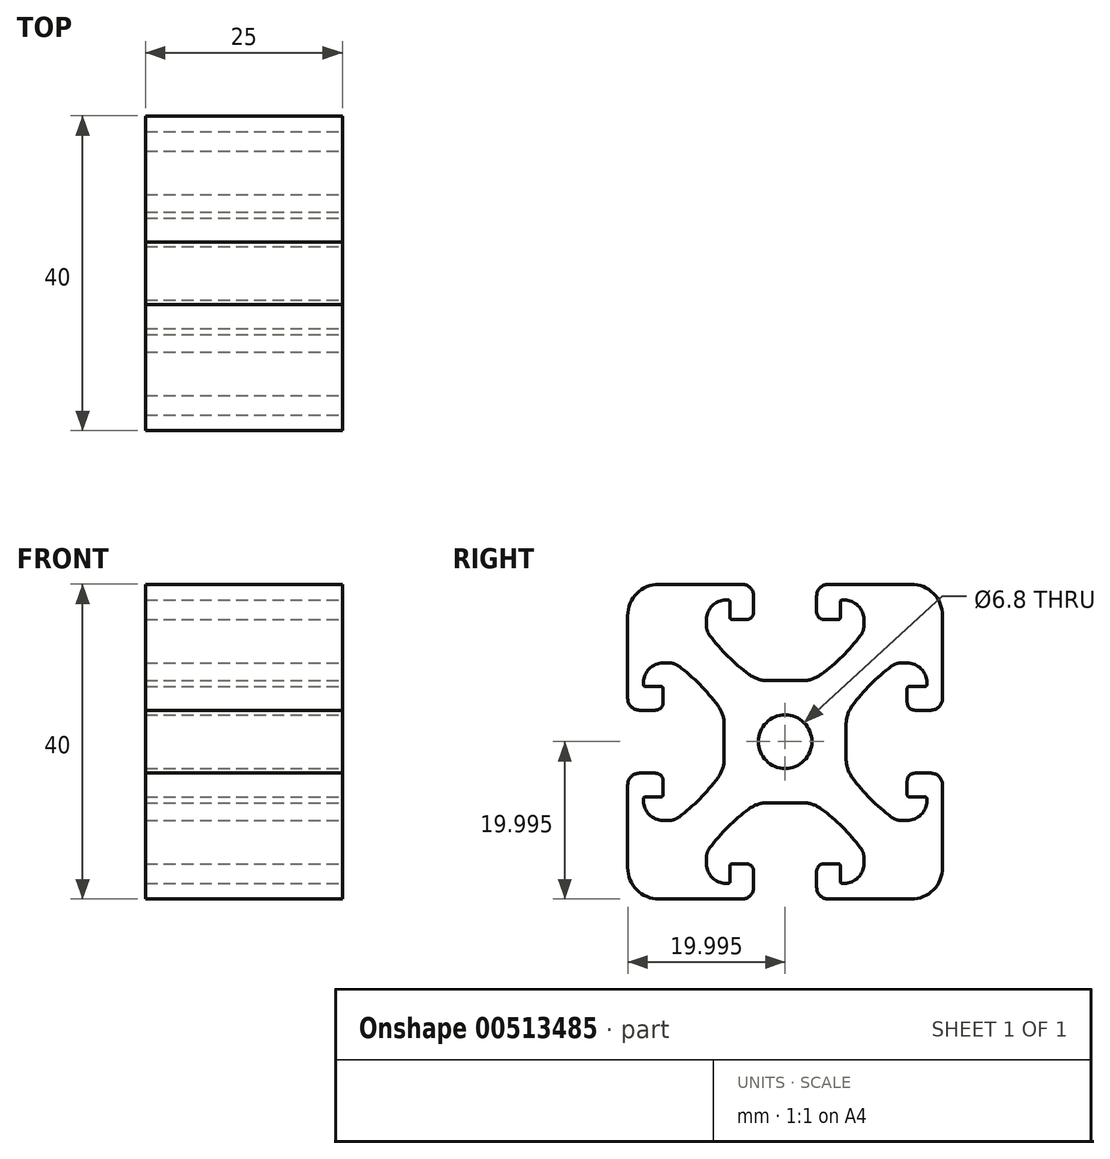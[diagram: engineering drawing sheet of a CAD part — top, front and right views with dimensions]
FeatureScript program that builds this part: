
annotation { "Feature Type Name" : "Feature", "Feature Type Description" : "" }
export const myFeature = defineFeature(function(context is Context, id is Id, definition is map)
    precondition{}
    {
        {
            var Q0;
            Q0=qCreatedBy(makeId("Right.planeOp"),FACE);
            var sketch = newSketch(context, id + "F0", { "sketchPlane" : qUnion([Q0])});
            skArc(sketch, "E0.0.0", {"start": v(4.09, -18.51) * mm, "mid": v(4.52, -19.58) * mm, "end": v(5.59, -20.01) * mm});
            skLineSegment(sketch, "E0.0.1", {"start": v(5.59, -20.01) * mm, "end": v(16.09, -20.01) * mm});
            skArc(sketch, "E0.0.2", {"start": v(16.09, -20.01) * mm, "mid": v(18.91, -18.84) * mm, "end": v(20.09, -16.01) * mm});
            skLineSegment(sketch, "E0.0.3", {"start": v(20.09, -16.01) * mm, "end": v(20.09, -5.51) * mm});
            skArc(sketch, "E0.0.4", {"start": v(20.09, -5.51) * mm, "mid": v(19.65, -4.45) * mm, "end": v(18.59, -4.01) * mm});
            skLineSegment(sketch, "E0.0.5", {"start": v(18.59, -4.01) * mm, "end": v(16.59, -4.01) * mm});
            skArc(sketch, "E0.0.6", {"start": v(16.59, -4.01) * mm, "mid": v(15.88, -4.3) * mm, "end": v(15.59, -5.01) * mm});
            skLineSegment(sketch, "E0.0.7", {"start": v(15.59, -5.01) * mm, "end": v(15.59, -6.76) * mm});
            skArc(sketch, "E0.0.8", {"start": v(15.59, -6.76) * mm, "mid": v(15.66, -6.94) * mm, "end": v(15.84, -7.01) * mm});
            skLineSegment(sketch, "E0.0.9", {"start": v(15.84, -7.01) * mm, "end": v(17.84, -7.01) * mm});
            skArc(sketch, "E0.0.10", {"start": v(17.84, -7.01) * mm, "mid": v(18.01, -7.09) * mm, "end": v(18.09, -7.26) * mm});
            skLineSegment(sketch, "E0.0.11", {"start": v(18.09, -7.26) * mm, "end": v(18.09, -7.51) * mm});
            skArc(sketch, "E0.0.12", {"start": v(18.09, -7.51) * mm, "mid": v(17.35, -9.28) * mm, "end": v(15.59, -10.01) * mm});
            skLineSegment(sketch, "E0.0.13", {"start": v(15.59, -10.01) * mm, "end": v(14.8, -10.01) * mm});
            skArc(sketch, "E0.0.14", {"start": v(14.8, -10.01) * mm, "mid": v(14.17, -9.91) * mm, "end": v(13.6, -9.6) * mm});
            skArc(sketch, "E0.0.15", {"start": v(13.6, -9.6) * mm, "mid": v(10.93, -7.28) * mm, "end": v(8.63, -4.6) * mm});
            skArc(sketch, "E0.0.16", {"start": v(8.63, -4.6) * mm, "mid": v(8.04, -3.47) * mm, "end": v(7.84, -2.2) * mm});
            skLineSegment(sketch, "E0.0.17", {"start": v(7.84, -2.2) * mm, "end": v(7.84, 2.18) * mm});
            skArc(sketch, "E0.0.18", {"start": v(7.84, 2.18) * mm, "mid": v(8.04, 3.44) * mm, "end": v(8.63, 4.57) * mm});
            skArc(sketch, "E0.0.19", {"start": v(8.63, 4.57) * mm, "mid": v(10.93, 7.25) * mm, "end": v(13.6, 9.58) * mm});
            skArc(sketch, "E0.0.20", {"start": v(13.6, 9.58) * mm, "mid": v(14.17, 9.88) * mm, "end": v(14.8, 9.99) * mm});
            skLineSegment(sketch, "E0.0.21", {"start": v(14.8, 9.99) * mm, "end": v(15.59, 9.99) * mm});
            skArc(sketch, "E0.0.22", {"start": v(15.59, 9.99) * mm, "mid": v(17.35, 9.25) * mm, "end": v(18.09, 7.49) * mm});
            skLineSegment(sketch, "E0.0.23", {"start": v(18.09, 7.49) * mm, "end": v(18.09, 7.24) * mm});
            skArc(sketch, "E0.0.24", {"start": v(18.09, 7.24) * mm, "mid": v(18.01, 7.06) * mm, "end": v(17.84, 6.99) * mm});
            skLineSegment(sketch, "E0.0.25", {"start": v(17.84, 6.99) * mm, "end": v(15.84, 6.99) * mm});
            skArc(sketch, "E0.0.26", {"start": v(15.84, 6.99) * mm, "mid": v(15.66, 6.91) * mm, "end": v(15.59, 6.74) * mm});
            skLineSegment(sketch, "E0.0.27", {"start": v(15.59, 6.74) * mm, "end": v(15.59, 4.99) * mm});
            skArc(sketch, "E0.0.28", {"start": v(15.59, 4.99) * mm, "mid": v(15.88, 4.28) * mm, "end": v(16.59, 3.99) * mm});
            skLineSegment(sketch, "E0.0.29", {"start": v(16.59, 3.99) * mm, "end": v(18.59, 3.99) * mm});
            skArc(sketch, "E0.0.30", {"start": v(18.59, 3.99) * mm, "mid": v(19.65, 4.42) * mm, "end": v(20.09, 5.49) * mm});
            skLineSegment(sketch, "E0.0.31", {"start": v(20.09, 5.49) * mm, "end": v(20.09, 15.99) * mm});
            skArc(sketch, "E0.0.32", {"start": v(20.09, 15.99) * mm, "mid": v(18.91, 18.81) * mm, "end": v(16.09, 19.99) * mm});
            skLineSegment(sketch, "E0.0.33", {"start": v(16.09, 19.99) * mm, "end": v(5.59, 19.99) * mm});
            skArc(sketch, "E0.0.34", {"start": v(5.59, 19.99) * mm, "mid": v(4.52, 19.55) * mm, "end": v(4.09, 18.49) * mm});
            skLineSegment(sketch, "E0.0.35", {"start": v(4.09, 18.49) * mm, "end": v(4.09, 16.49) * mm});
            skArc(sketch, "E0.0.36", {"start": v(4.09, 16.49) * mm, "mid": v(4.38, 15.78) * mm, "end": v(5.09, 15.49) * mm});
            skLineSegment(sketch, "E0.0.37", {"start": v(5.09, 15.49) * mm, "end": v(6.84, 15.49) * mm});
            skArc(sketch, "E0.0.38", {"start": v(6.84, 15.49) * mm, "mid": v(7.01, 15.56) * mm, "end": v(7.09, 15.74) * mm});
            skLineSegment(sketch, "E0.0.39", {"start": v(7.09, 15.74) * mm, "end": v(7.09, 17.74) * mm});
            skArc(sketch, "E0.0.40", {"start": v(7.09, 17.74) * mm, "mid": v(7.16, 17.91) * mm, "end": v(7.34, 17.99) * mm});
            skLineSegment(sketch, "E0.0.41", {"start": v(7.34, 17.99) * mm, "end": v(7.59, 17.99) * mm});
            skArc(sketch, "E0.0.42", {"start": v(7.59, 17.99) * mm, "mid": v(9.35, 17.25) * mm, "end": v(10.09, 15.49) * mm});
            skLineSegment(sketch, "E0.0.43", {"start": v(10.09, 15.49) * mm, "end": v(10.09, 14.7) * mm});
            skArc(sketch, "E0.0.44", {"start": v(10.09, 14.7) * mm, "mid": v(9.98, 14.07) * mm, "end": v(9.68, 13.5) * mm});
            skArc(sketch, "E0.0.45", {"start": v(9.68, 13.5) * mm, "mid": v(7.35, 10.83) * mm, "end": v(4.67, 8.53) * mm});
            skArc(sketch, "E0.0.46", {"start": v(4.67, 8.53) * mm, "mid": v(3.54, 7.94) * mm, "end": v(2.28, 7.74) * mm});
            skLineSegment(sketch, "E0.0.47", {"start": v(2.28, 7.74) * mm, "end": v(-2.1, 7.74) * mm});
            skArc(sketch, "E0.0.48", {"start": v(-2.1, 7.74) * mm, "mid": v(-3.37, 7.94) * mm, "end": v(-4.5, 8.53) * mm});
            skArc(sketch, "E0.0.49", {"start": v(-4.5, 8.53) * mm, "mid": v(-7.18, 10.83) * mm, "end": v(-9.5, 13.5) * mm});
            skArc(sketch, "E0.0.50", {"start": v(-9.5, 13.5) * mm, "mid": v(-9.81, 14.07) * mm, "end": v(-9.91, 14.7) * mm});
            skLineSegment(sketch, "E0.0.51", {"start": v(-9.91, 14.7) * mm, "end": v(-9.91, 15.49) * mm});
            skArc(sketch, "E0.0.52", {"start": v(-9.91, 15.49) * mm, "mid": v(-9.18, 17.25) * mm, "end": v(-7.41, 17.99) * mm});
            skLineSegment(sketch, "E0.0.53", {"start": v(-7.41, 17.99) * mm, "end": v(-7.16, 17.99) * mm});
            skArc(sketch, "E0.0.54", {"start": v(-7.16, 17.99) * mm, "mid": v(-6.99, 17.91) * mm, "end": v(-6.91, 17.74) * mm});
            skLineSegment(sketch, "E0.0.55", {"start": v(-6.91, 17.74) * mm, "end": v(-6.91, 15.74) * mm});
            skArc(sketch, "E0.0.56", {"start": v(-6.91, 15.74) * mm, "mid": v(-6.84, 15.56) * mm, "end": v(-6.66, 15.49) * mm});
            skLineSegment(sketch, "E0.0.57", {"start": v(-6.66, 15.49) * mm, "end": v(-4.91, 15.49) * mm});
            skArc(sketch, "E0.0.58", {"start": v(-4.91, 15.49) * mm, "mid": v(-4.2, 15.78) * mm, "end": v(-3.91, 16.49) * mm});
            skLineSegment(sketch, "E0.0.59", {"start": v(-3.91, 16.49) * mm, "end": v(-3.91, 18.49) * mm});
            skArc(sketch, "E0.0.60", {"start": v(-3.91, 18.49) * mm, "mid": v(-4.35, 19.55) * mm, "end": v(-5.41, 19.99) * mm});
            skLineSegment(sketch, "E0.0.61", {"start": v(-5.41, 19.99) * mm, "end": v(-15.91, 19.99) * mm});
            skArc(sketch, "E0.0.62", {"start": v(-15.91, 19.99) * mm, "mid": v(-18.74, 18.81) * mm, "end": v(-19.91, 15.99) * mm});
            skLineSegment(sketch, "E0.0.63", {"start": v(-19.91, 15.99) * mm, "end": v(-19.91, 5.49) * mm});
            skArc(sketch, "E0.0.64", {"start": v(-19.91, 5.49) * mm, "mid": v(-19.48, 4.42) * mm, "end": v(-18.41, 3.99) * mm});
            skLineSegment(sketch, "E0.0.65", {"start": v(-18.41, 3.99) * mm, "end": v(-16.41, 3.99) * mm});
            skArc(sketch, "E0.0.66", {"start": v(-16.41, 3.99) * mm, "mid": v(-15.7, 4.28) * mm, "end": v(-15.41, 4.99) * mm});
            skLineSegment(sketch, "E0.0.67", {"start": v(-15.41, 4.99) * mm, "end": v(-15.41, 6.74) * mm});
            skArc(sketch, "E0.0.68", {"start": v(-15.41, 6.74) * mm, "mid": v(-15.49, 6.91) * mm, "end": v(-15.66, 6.99) * mm});
            skLineSegment(sketch, "E0.0.69", {"start": v(-15.66, 6.99) * mm, "end": v(-17.66, 6.99) * mm});
            skArc(sketch, "E0.0.70", {"start": v(-17.66, 6.99) * mm, "mid": v(-17.84, 7.06) * mm, "end": v(-17.91, 7.24) * mm});
            skLineSegment(sketch, "E0.0.71", {"start": v(-17.91, 7.24) * mm, "end": v(-17.91, 7.49) * mm});
            skArc(sketch, "E0.0.72", {"start": v(-17.91, 7.49) * mm, "mid": v(-17.18, 9.25) * mm, "end": v(-15.41, 9.99) * mm});
            skLineSegment(sketch, "E0.0.73", {"start": v(-15.41, 9.99) * mm, "end": v(-14.64, 9.99) * mm});
            skArc(sketch, "E0.0.74", {"start": v(-14.64, 9.99) * mm, "mid": v(-14, 9.88) * mm, "end": v(-13.43, 9.58) * mm});
            skArc(sketch, "E0.0.75", {"start": v(-13.43, 9.58) * mm, "mid": v(-10.76, 7.25) * mm, "end": v(-8.46, 4.57) * mm});
            skArc(sketch, "E0.0.76", {"start": v(-8.46, 4.57) * mm, "mid": v(-7.87, 3.44) * mm, "end": v(-7.66, 2.18) * mm});
            skLineSegment(sketch, "E0.0.77", {"start": v(-7.66, 2.18) * mm, "end": v(-7.66, -2.2) * mm});
            skArc(sketch, "E0.0.78", {"start": v(-7.66, -2.2) * mm, "mid": v(-7.87, -3.47) * mm, "end": v(-8.46, -4.6) * mm});
            skArc(sketch, "E0.0.79", {"start": v(-8.46, -4.6) * mm, "mid": v(-10.76, -7.28) * mm, "end": v(-13.43, -9.6) * mm});
            skArc(sketch, "E0.0.80", {"start": v(-13.43, -9.6) * mm, "mid": v(-14, -9.91) * mm, "end": v(-14.64, -10.01) * mm});
            skLineSegment(sketch, "E0.0.81", {"start": v(-14.64, -10.01) * mm, "end": v(-15.41, -10.01) * mm});
            skArc(sketch, "E0.0.82", {"start": v(-15.41, -10.01) * mm, "mid": v(-17.18, -9.28) * mm, "end": v(-17.91, -7.51) * mm});
            skLineSegment(sketch, "E0.0.83", {"start": v(-17.91, -7.51) * mm, "end": v(-17.91, -7.26) * mm});
            skArc(sketch, "E0.0.84", {"start": v(-17.91, -7.26) * mm, "mid": v(-17.84, -7.09) * mm, "end": v(-17.66, -7.01) * mm});
            skLineSegment(sketch, "E0.0.85", {"start": v(-17.66, -7.01) * mm, "end": v(-15.66, -7.01) * mm});
            skArc(sketch, "E0.0.86", {"start": v(-15.66, -7.01) * mm, "mid": v(-15.49, -6.94) * mm, "end": v(-15.41, -6.76) * mm});
            skLineSegment(sketch, "E0.0.87", {"start": v(-15.41, -6.76) * mm, "end": v(-15.41, -5.01) * mm});
            skArc(sketch, "E0.0.88", {"start": v(-15.41, -5.01) * mm, "mid": v(-15.7, -4.3) * mm, "end": v(-16.41, -4.01) * mm});
            skLineSegment(sketch, "E0.0.89", {"start": v(-16.41, -4.01) * mm, "end": v(-18.41, -4.01) * mm});
            skArc(sketch, "E0.0.90", {"start": v(-18.41, -4.01) * mm, "mid": v(-19.48, -4.45) * mm, "end": v(-19.91, -5.51) * mm});
            skLineSegment(sketch, "E0.0.91", {"start": v(-19.91, -5.51) * mm, "end": v(-19.91, -16.01) * mm});
            skArc(sketch, "E0.0.92", {"start": v(-19.91, -16.01) * mm, "mid": v(-18.74, -18.84) * mm, "end": v(-15.91, -20.01) * mm});
            skLineSegment(sketch, "E0.0.93", {"start": v(-15.91, -20.01) * mm, "end": v(-5.41, -20.01) * mm});
            skArc(sketch, "E0.0.94", {"start": v(-5.41, -20.01) * mm, "mid": v(-4.35, -19.58) * mm, "end": v(-3.91, -18.51) * mm});
            skLineSegment(sketch, "E0.0.95", {"start": v(-3.91, -18.51) * mm, "end": v(-3.91, -16.51) * mm});
            skArc(sketch, "E0.0.96", {"start": v(-3.91, -16.51) * mm, "mid": v(-4.2, -15.8) * mm, "end": v(-4.91, -15.51) * mm});
            skLineSegment(sketch, "E0.0.97", {"start": v(-4.91, -15.51) * mm, "end": v(-6.66, -15.51) * mm});
            skArc(sketch, "E0.0.98", {"start": v(-6.66, -15.51) * mm, "mid": v(-6.84, -15.59) * mm, "end": v(-6.91, -15.76) * mm});
            skLineSegment(sketch, "E0.0.99", {"start": v(-6.91, -15.76) * mm, "end": v(-6.91, -17.76) * mm});
            skArc(sketch, "E0.0.100", {"start": v(-6.91, -17.76) * mm, "mid": v(-6.99, -17.94) * mm, "end": v(-7.16, -18.01) * mm});
            skLineSegment(sketch, "E0.0.101", {"start": v(-7.16, -18.01) * mm, "end": v(-7.41, -18.01) * mm});
            skArc(sketch, "E0.0.102", {"start": v(-7.41, -18.01) * mm, "mid": v(-9.18, -17.28) * mm, "end": v(-9.91, -15.51) * mm});
            skLineSegment(sketch, "E0.0.103", {"start": v(-9.91, -15.51) * mm, "end": v(-9.91, -14.73) * mm});
            skArc(sketch, "E0.0.104", {"start": v(-9.91, -14.73) * mm, "mid": v(-9.81, -14.1) * mm, "end": v(-9.5, -13.53) * mm});
            skArc(sketch, "E0.0.105", {"start": v(-9.5, -13.53) * mm, "mid": v(-7.18, -10.86) * mm, "end": v(-4.5, -8.56) * mm});
            skArc(sketch, "E0.0.106", {"start": v(-4.5, -8.56) * mm, "mid": v(-3.37, -7.97) * mm, "end": v(-2.1, -7.76) * mm});
            skLineSegment(sketch, "E0.0.107", {"start": v(-2.1, -7.76) * mm, "end": v(2.28, -7.76) * mm});
            skArc(sketch, "E0.0.108", {"start": v(2.28, -7.76) * mm, "mid": v(3.54, -7.97) * mm, "end": v(4.67, -8.56) * mm});
            skArc(sketch, "E0.0.109", {"start": v(4.67, -8.56) * mm, "mid": v(7.35, -10.86) * mm, "end": v(9.68, -13.53) * mm});
            skArc(sketch, "E0.0.110", {"start": v(9.68, -13.53) * mm, "mid": v(9.98, -14.1) * mm, "end": v(10.09, -14.73) * mm});
            skLineSegment(sketch, "E0.0.111", {"start": v(10.09, -14.73) * mm, "end": v(10.09, -15.51) * mm});
            skArc(sketch, "E0.0.112", {"start": v(10.09, -15.51) * mm, "mid": v(9.35, -17.28) * mm, "end": v(7.59, -18.01) * mm});
            skLineSegment(sketch, "E0.0.113", {"start": v(7.59, -18.01) * mm, "end": v(7.34, -18.01) * mm});
            skArc(sketch, "E0.0.114", {"start": v(7.34, -18.01) * mm, "mid": v(7.16, -17.94) * mm, "end": v(7.09, -17.76) * mm});
            skLineSegment(sketch, "E0.0.115", {"start": v(7.09, -17.76) * mm, "end": v(7.09, -15.76) * mm});
            skArc(sketch, "E0.0.116", {"start": v(7.09, -15.76) * mm, "mid": v(7.01, -15.59) * mm, "end": v(6.84, -15.51) * mm});
            skLineSegment(sketch, "E0.0.117", {"start": v(6.84, -15.51) * mm, "end": v(5.09, -15.51) * mm});
            skArc(sketch, "E0.0.118", {"start": v(5.09, -15.51) * mm, "mid": v(4.38, -15.8) * mm, "end": v(4.09, -16.51) * mm});
            skLineSegment(sketch, "E0.0.119", {"start": v(4.09, -16.51) * mm, "end": v(4.09, -18.51) * mm});
            skCircle(sketch, "E1.0", {"center": v(0.09, -0.01) * mm, "radius": 3.4 * mm});
            skSolve(sketch);
        }
        {
            var Q0;
            Q0=makeQuery(id+"F0.imprint","IMPRINT",FACE,{"disambiguationData":[TD([[makeQuery(id+"F0.imprint","IMPRINT",EDGE,{"derivedFrom":sQuery(id+"F0.wireOp",EDGE,"E0.0.0")}),1.0]])]});
            extrude(context, id + "F1", {"entities" : qUnion([Q0]), "oppositeDirection" : true, "depth" : 25 * mm, "offsetDistance" : 25 * mm});
        }
    });
